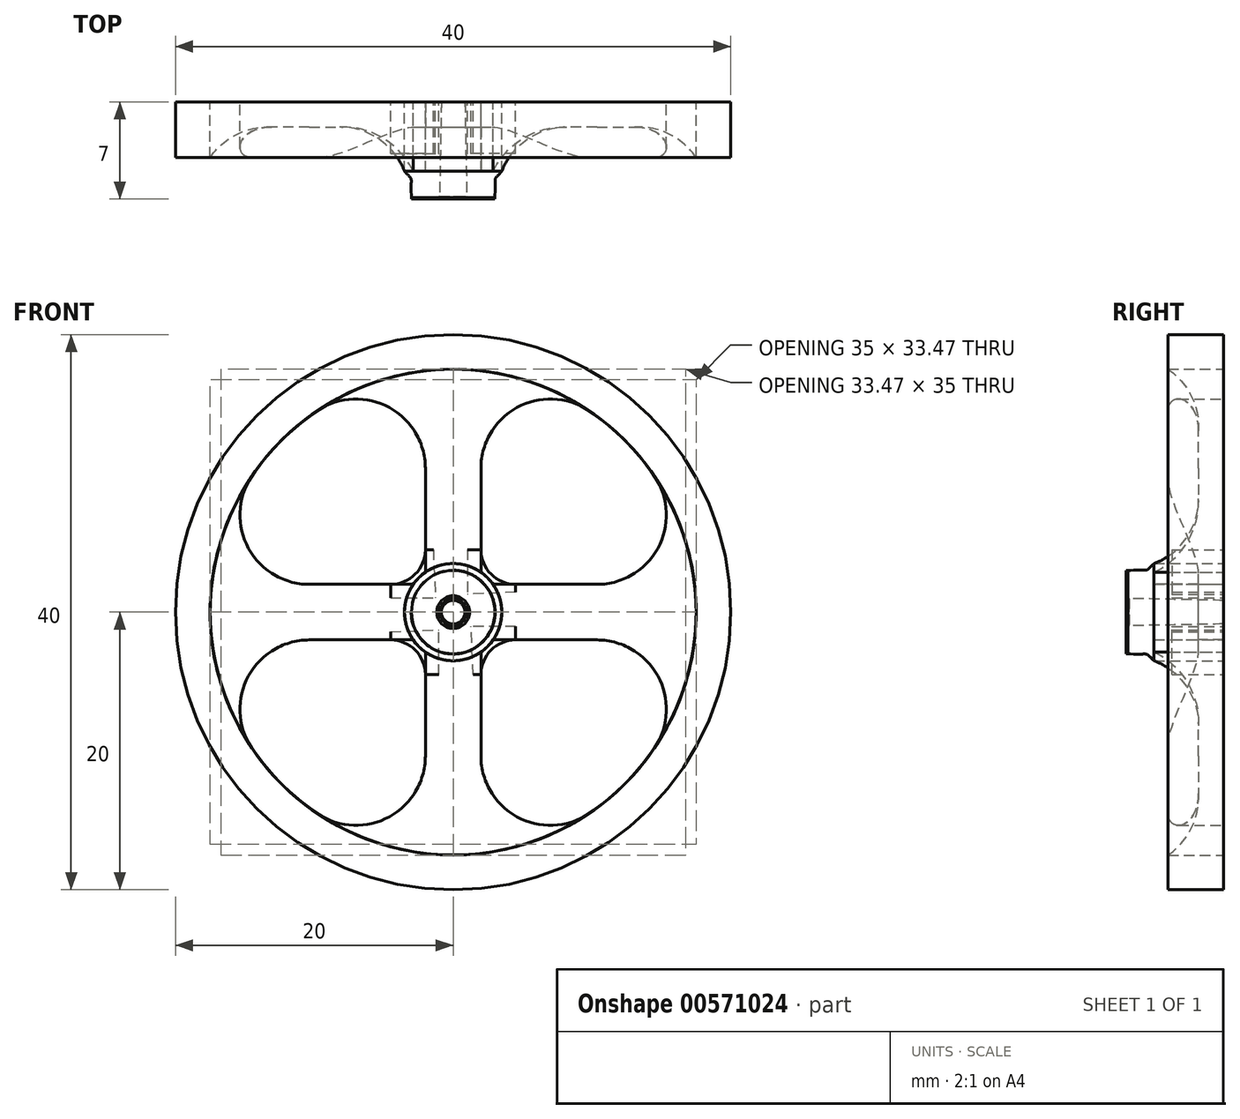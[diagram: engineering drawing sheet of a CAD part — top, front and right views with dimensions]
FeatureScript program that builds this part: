
annotation { "Feature Type Name" : "Feature", "Feature Type Description" : "" }
export const myFeature = defineFeature(function(context is Context, id is Id, definition is map)
    precondition{}
    {
        {
            var Q0;
            Q0=qCreatedBy(makeId("Front.planeOp"),FACE);
            var sketch = newSketch(context, id + "F0", { "sketchPlane" : qUnion([Q0])});
            skCircle(sketch, "E0", {"center": v(0, 0) * mm, "radius": 3.5 * mm});
            skSolve(sketch);
        }
        {
            var Q0;
            Q0=qSketchRegion(id+"F0",true);
            extrude(context, id + "F1", {"entities" : qUnion([Q0]), "depth" : 5 * mm, "offsetDistance" : 25 * mm});
        }
        {
            var Q0;
            Q0=qCreatedBy(makeId("Right.planeOp"),FACE);
            var sketch = newSketch(context, id + "F2", { "sketchPlane" : qUnion([Q0])});
            skLineSegment(sketch, "E1", {"start": v(3.77, 0) * mm, "end": v(-36.31, 0) * mm, "construction": true});
            skLineSegment(sketch, "E2", {"start": v(-7, 0) * mm, "end": v(-7, 3) * mm});
            skLineSegment(sketch, "E3", {"start": v(-7, 3) * mm, "end": v(-6.9, 3) * mm});
            skFitSpline(sketch, "E4", {"points": [v(-6.9, 3) * mm, v(-5, 3.5) * mm], "startDerivative": vector(5.34, 0.31) * mm, "endDerivative": vector(2.38, 2.14) * mm});
            skLineSegment(sketch, "E5", {"start": v(-5, 3.5) * mm, "end": v(-5, 0) * mm});
            skLineSegment(sketch, "E6", {"start": v(-5, 0) * mm, "end": v(-7, 0) * mm});
            skSolve(sketch);
        }
        {
            var Q0;
            Q0=qSketchRegion(id+"F2",true);
            var Q1;
            Q1=sQuery(id+"F2.wireOp",EDGE,"E1");
            revolve(context, id + "F3", {"operationType" : NewBodyOperationType.ADD, "entities" : qUnion([Q0]), "axis" : qUnion([Q1]), "revolveType" : RevolveType.FULL});
        }
        {
            var Q0;
            Q0=makeQuery(id+"F1.opExtrude","CAP_FACE",FACE,{"disambiguationData":[OSD([sQuery(id+"F0.wireOp",EDGE,"E0")])],"isStart":true});
            var sketch = newSketch(context, id + "F4", { "sketchPlane" : qUnion([Q0])});
            skCircle(sketch, "E7", {"center": v(0, 0) * mm, "radius": 0.85 * mm});
            skSolve(sketch);
        }
        {
            var Q0;
            Q0=qSketchRegion(id+"F4",true);
            extrude(context, id + "F5", {"entities" : qUnion([Q0]), "operationType" : NewBodyOperationType.REMOVE, "endBound" : BoundingType.THROUGH_ALL, "oppositeDirection" : true, "depth" : 25 * mm, "hasDraft" : true, "draftAngle" : 1.1 * degree, "offsetDistance" : 25 * mm});
        }
        {
            var Q0;
            Q0=qCreatedBy(makeId("Top.planeOp"),FACE);
            var sketch = newSketch(context, id + "F6", { "sketchPlane" : qUnion([Q0])});
            skLineSegment(sketch, "E8.bottom", {"start": v(-2, 0) * mm, "end": v(2, 0) * mm});
            skLineSegment(sketch, "E8.top", {"start": v(-2, -1.8) * mm, "end": v(2, -1.8) * mm});
            skLineSegment(sketch, "E8.left", {"start": v(-2, 0) * mm, "end": v(-2, -1.8) * mm});
            skLineSegment(sketch, "E8.right", {"start": v(2, 0) * mm, "end": v(2, -1.8) * mm});
            skSolve(sketch);
        }
        {
            var Q0;
            Q0=qSketchRegion(id+"F6",true);
            extrude(context, id + "F7", {"entities" : qUnion([Q0]), "operationType" : NewBodyOperationType.ADD, "depth" : 18 * mm, "hasSecondDirection" : true, "secondDirectionOppositeDirection" : false, "secondDirectionDepth" : 2.5 * mm, "offsetDistance" : 25 * mm});
        }
        {
            var Q0;
            Q0=makeQuery(id+"F5.boolean.opBoolean","INTERSECT",EDGE,{"derivedFrom":[makeQuery(id+"F3.opRevolve","SWEPT_FACE",FACE,{"disambiguationData":[OSD([sQuery(id+"F2.wireOp",EDGE,"E2")])]}),makeQuery(id+"F5.opExtrude","SWEPT_FACE",FACE,{"disambiguationData":[OSD([sQuery(id+"F4.wireOp",EDGE,"E7")])]})]});
            chamfer(context, id + "F8", {"entities" : qUnion([Q0]), "width" : .2 * mm, "tangentPropagation" : true});
        }
        {
            var Q0;
            Q0=makeQuery(id+"F7.boolean.opBoolean","MERGE",FACE,{"derivedFrom":[makeQuery(id+"F1.opExtrude","CAP_FACE",FACE,{"disambiguationData":[OSD([sQuery(id+"F0.wireOp",EDGE,"E0")])],"isStart":true}),makeQuery(id+"F7.opExtrude","SWEPT_FACE",FACE,{"disambiguationData":[OSD([sQuery(id+"F6.wireOp",EDGE,"E8.bottom")])]})]});
            var sketch = newSketch(context, id + "F9", { "sketchPlane" : qUnion([Q0])});
            skCircle(sketch, "E9", {"center": v(0, 0) * mm, "radius": 20 * mm});
            skCircle(sketch, "E10", {"center": v(0, 0) * mm, "radius": 17.5 * mm});
            skSolve(sketch);
        }
        {
            var Q0;
            Q0=qSketchRegion(id+"F9",true);
            extrude(context, id + "F10", {"entities" : qUnion([Q0]), "operationType" : NewBodyOperationType.ADD, "oppositeDirection" : true, "depth" : 4 * mm, "offsetDistance" : 25 * mm});
        }
        {
            var Q0;
            Q0=makeQuery(id+"F7.boolean.opBoolean","INTERSECT",EDGE,{"derivedFrom":[makeQuery(id+"F1.opExtrude","SWEPT_FACE",FACE,{"disambiguationData":[OSD([sQuery(id+"F0.wireOp",EDGE,"E0")])]}),makeQuery(id+"F7.opExtrude","SWEPT_FACE",FACE,{"disambiguationData":[OSD([sQuery(id+"F6.wireOp",EDGE,"E8.top")])]})]});
            var Q1;
            Q1=makeQuery(id+"F10.boolean.opBoolean","INTERSECT",EDGE,{"derivedFrom":[makeQuery(id+"F7.opExtrude","SWEPT_FACE",FACE,{"disambiguationData":[OSD([sQuery(id+"F6.wireOp",EDGE,"E8.top")])]}),makeQuery(id+"F10.opExtrude","SWEPT_FACE",FACE,{"disambiguationData":[OSD([sQuery(id+"F9.wireOp",EDGE,"E10")])]})]});
            fillet(context, id + "F11", {"entities" : qUnion([Q0, Q1]), "radius" : 5 * mm, "tangentPropagation" : true, "allowEdgeOverflow" : false});
        }
        {
            var Q0;
            Q0=makeQuery(id+"F10.boolean.opBoolean","INTERSECT",EDGE,{"derivedFrom":[makeQuery(id+"F7.opExtrude","SWEPT_FACE",FACE,{"disambiguationData":[OSD([sQuery(id+"F6.wireOp",EDGE,"E8.right")])]}),makeQuery(id+"F10.opExtrude","SWEPT_FACE",FACE,{"disambiguationData":[OSD([sQuery(id+"F9.wireOp",EDGE,"E10")])]})]});
            var Q1;
            Q1=makeQuery(id+"F10.boolean.opBoolean","INTERSECT",EDGE,{"derivedFrom":[makeQuery(id+"F7.opExtrude","SWEPT_FACE",FACE,{"disambiguationData":[OSD([sQuery(id+"F6.wireOp",EDGE,"E8.left")])]}),makeQuery(id+"F10.opExtrude","SWEPT_FACE",FACE,{"disambiguationData":[OSD([sQuery(id+"F9.wireOp",EDGE,"E10")])]})]});
            fillet(context, id + "F12", {"entities" : qUnion([Q0, Q1]), "radius" : 5 * mm, "tangentPropagation" : true, "allowEdgeOverflow" : false});
        }
        {
            var Q0;
            Q0=makeQuery(id+"F1.opExtrude","SWEPT_BODY",BODY,{"disambiguationData":[OSD([sQuery(id+"F0.wireOp",EDGE,"E0")])]});
            var Q1;
            Q1=makeQuery(id+"F3.opRevolve","SWEPT_FACE",FACE,{"disambiguationData":[OSD([sQuery(id+"F2.wireOp",EDGE,"E3")])]});
            circularPattern(context, id + "F13", {"entities" : qUnion([Q0]), "axis" : qUnion([Q1]), "angle" : 360 * degree, "instanceCount" : 4, "equalSpace" : true});
        }
        {
            var Q0;
            {var subQ0=makeQuery(id+"F10.boolean.opBoolean","MERGE",FACE,{"derivedFrom":[makeQuery(id+"F7.boolean.opBoolean","MERGE",FACE,{"derivedFrom":[makeQuery(id+"F1.opExtrude","CAP_FACE",FACE,{"disambiguationData":[OSD([sQuery(id+"F0.wireOp",EDGE,"E0")])],"isStart":true}),makeQuery(id+"F7.opExtrude","SWEPT_FACE",FACE,{"disambiguationData":[OSD([sQuery(id+"F6.wireOp",EDGE,"E8.bottom")])]})]}),makeQuery(id+"F10.opExtrude","CAP_FACE",FACE,{"disambiguationData":[OSD([sQuery(id+"F9.wireOp",EDGE,"E9"),sQuery(id+"F9.wireOp",EDGE,"E10")])],"isStart":true})]});Q0=makeQuery(id+"FgIhm2Tt6zTOsJ9_1.boolean.opBoolean","MERGE",FACE,{"derivedFrom":[makeQuery(id+"FDYBKFrb20v7z53_1.opBoolean","MERGE",FACE,{"derivedFrom":[subQ0,makeQuery(id+"F13.opPattern","COPY",FACE,{"derivedFrom":subQ0,"instanceName":"1"}),makeQuery(id+"F13.opPattern","COPY",FACE,{"derivedFrom":subQ0,"instanceName":"2"}),makeQuery(id+"F13.opPattern","COPY",FACE,{"derivedFrom":subQ0,"instanceName":"3"})]}),makeQuery(id+"FgIhm2Tt6zTOsJ9_1.opExtrude","CAP_FACE",FACE,{"disambiguationData":[OSD([sQuery(id+"FTYQuE2zEAQoyuF_1.wireOp",EDGE,"2QqTN2Jg-TwYb-xefx-Ns2m-0Et6M2J3xaq2"),sQuery(id+"FTYQuE2zEAQoyuF_1.wireOp",EDGE,"eRERD4EF-URZr-QwCf-6lY6-XNeSWXYZj7bk"),sQuery(id+"FTYQuE2zEAQoyuF_1.wireOp",EDGE,"w1udHuFG-gaxB-rpRy-TvAe-Q6hEAi3vOdkO"),sQuery(id+"FTYQuE2zEAQoyuF_1.wireOp",EDGE,"ccb8e607-9a5f-4511-8021-514936b70c73.filletArc"),sQuery(id+"FTYQuE2zEAQoyuF_1.wireOp",EDGE,"0a0adc1d-e557-4132-b897-d3ac198357fb.filletArc"),sQuery(id+"FTYQuE2zEAQoyuF_1.wireOp",EDGE,"b0aMqVTr-uXCx-4wKI-6uIc-G6YGe43DG1Aq"),sQuery(id+"FTYQuE2zEAQoyuF_1.wireOp",EDGE,"I1tABSEo-hI8d-lGJT-UJOT-oiTtTxIxys52"),sQuery(id+"FTYQuE2zEAQoyuF_1.wireOp",EDGE,"LAcF6vfi-sfcO-sjto-NgG3-pIlErQrigMXa"),sQuery(id+"FTYQuE2zEAQoyuF_1.wireOp",EDGE,"aqtcTmt6-T24C-q2HQ-cTpA-Y39zHsUlbNQ4")])],"isStart":true})]});}
            var sketch = newSketch(context, id + "F14", { "sketchPlane" : qUnion([Q0])});
            skArc(sketch, "E11", {"start": v(-4.5, 2) * mm, "mid": v(-2.73, 2.73) * mm, "end": v(-2, 4.5) * mm});
            skLineSegment(sketch, "E12", {"start": v(-2, 4.5) * mm, "end": v(-1.03, 4.5) * mm});
            skLineSegment(sketch, "E13", {"start": v(-1.03, 4.5) * mm, "end": v(-1.03, 1.28) * mm});
            skLineSegment(sketch, "E14", {"start": v(-4.5, 2) * mm, "end": v(-4.5, 1.43) * mm});
            skLineSegment(sketch, "E15", {"start": v(-4.5, 1.43) * mm, "end": v(-1.03, 1.28) * mm});
            skLineSegment(sketch, "E16.1.0", {"start": v(-4.5, -2) * mm, "end": v(-4.5, -1.03) * mm});
            skLineSegment(sketch, "E16.1.1", {"start": v(-4.5, -1.03) * mm, "end": v(-1.28, -1.03) * mm});
            skLineSegment(sketch, "E16.1.2", {"start": v(-1.43, -4.5) * mm, "end": v(-1.28, -1.03) * mm});
            skLineSegment(sketch, "E16.1.3", {"start": v(-2, -4.5) * mm, "end": v(-1.43, -4.5) * mm});
            skArc(sketch, "E16.1.4", {"start": v(-2, -4.5) * mm, "mid": v(-2.73, -2.73) * mm, "end": v(-4.5, -2) * mm});
            skLineSegment(sketch, "E16.2.0", {"start": v(2, -4.5) * mm, "end": v(1.03, -4.5) * mm});
            skLineSegment(sketch, "E16.2.1", {"start": v(1.03, -4.5) * mm, "end": v(1.03, -1.28) * mm});
            skLineSegment(sketch, "E16.2.2", {"start": v(4.5, -1.43) * mm, "end": v(1.03, -1.28) * mm});
            skLineSegment(sketch, "E16.2.3", {"start": v(4.5, -2) * mm, "end": v(4.5, -1.43) * mm});
            skArc(sketch, "E16.2.4", {"start": v(4.5, -2) * mm, "mid": v(2.73, -2.73) * mm, "end": v(2, -4.5) * mm});
            skLineSegment(sketch, "E16.3.0", {"start": v(4.5, 2) * mm, "end": v(4.5, 1.03) * mm});
            skLineSegment(sketch, "E16.3.1", {"start": v(4.5, 1.03) * mm, "end": v(1.28, 1.03) * mm});
            skLineSegment(sketch, "E16.3.2", {"start": v(1.43, 4.5) * mm, "end": v(1.28, 1.03) * mm});
            skLineSegment(sketch, "E16.3.3", {"start": v(2, 4.5) * mm, "end": v(1.43, 4.5) * mm});
            skArc(sketch, "E16.3.4", {"start": v(2, 4.5) * mm, "mid": v(2.73, 2.73) * mm, "end": v(4.5, 2) * mm});
            skPoint(sketch, "E16.center", {"position": v(0, 0) * mm});
            skSolve(sketch);
        }
        {
            var Q0;
            Q0=qSketchRegion(id+"F14",true);
            extrude(context, id + "F15", {"entities" : qUnion([Q0]), "oppositeDirection" : true, "depth" : 3.7 * mm});
        }
    });
